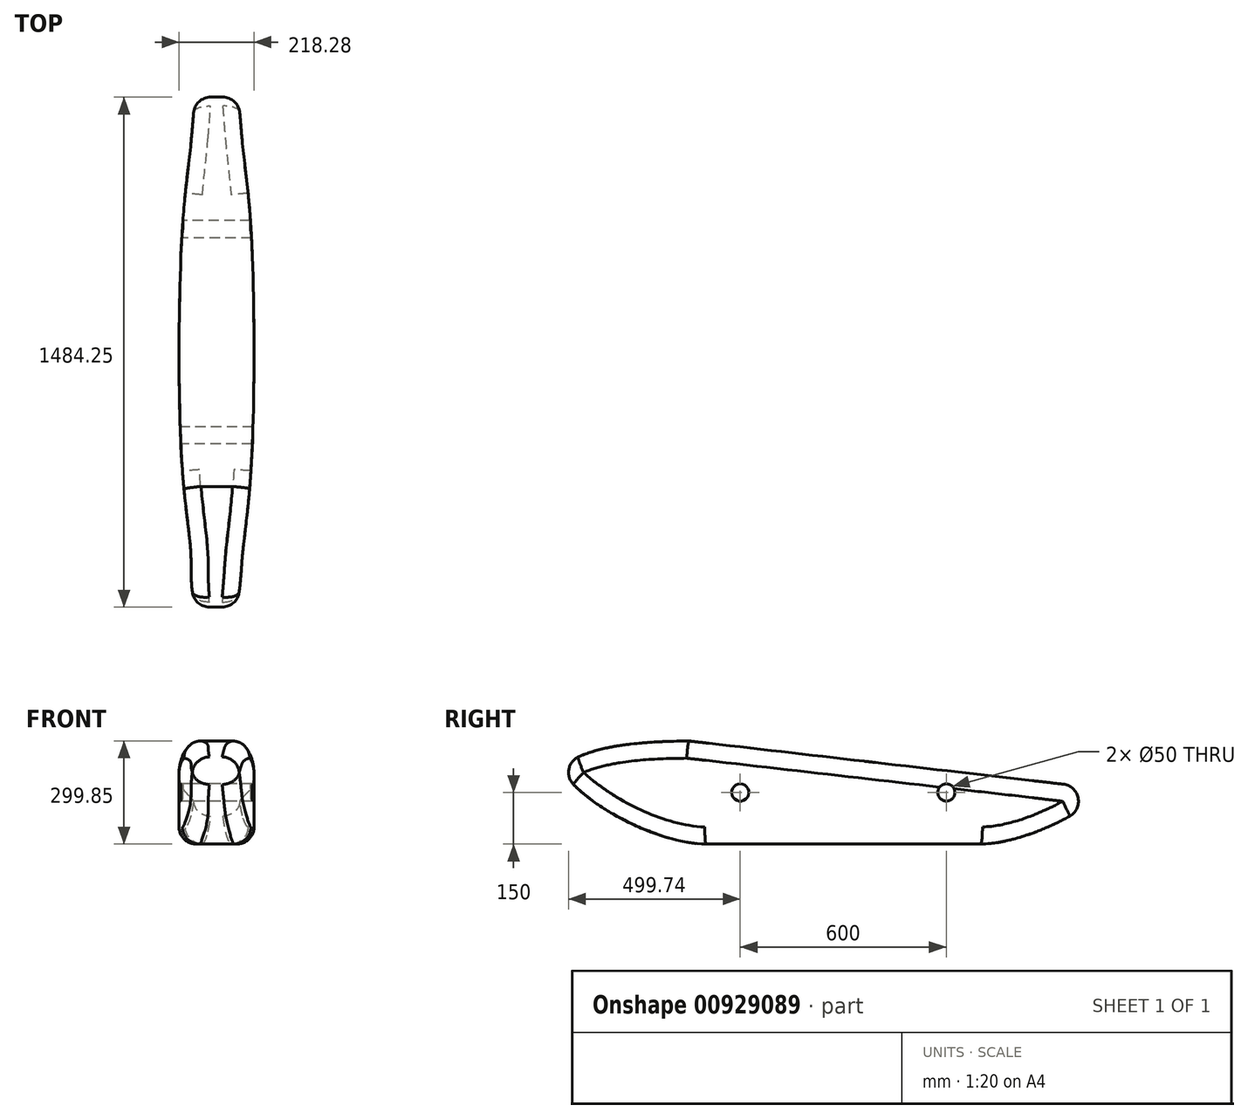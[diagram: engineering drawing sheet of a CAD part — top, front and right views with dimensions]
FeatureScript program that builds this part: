
annotation { "Feature Type Name" : "Feature", "Feature Type Description" : "" }
export const myFeature = defineFeature(function(context is Context, id is Id, definition is map)
    precondition{}
    {
        {
            var Q0;
            Q0=qCreatedBy(makeId("Top.planeOp"),FACE);
            var sketch = newSketch(context, id + "F0", { "sketchPlane" : qUnion([Q0])});
            skLineSegment(sketch, "E0", {"start": v(0, 0) * mm, "end": v(0, -1700) * mm});
            skLineSegment(sketch, "E1", {"start": v(-75, -300) * mm, "end": v(75, -300) * mm});
            skLineSegment(sketch, "E2", {"start": v(-75, -1500) * mm, "end": v(75, -1500) * mm});
            skLineSegment(sketch, "E3", {"start": v(-100, -550) * mm, "end": v(100, -550) * mm});
            skLineSegment(sketch, "E4", {"start": v(-100, -1250) * mm, "end": v(100, -1250) * mm});
            skLineSegment(sketch, "E5", {"start": v(-50, 0) * mm, "end": v(50, 0) * mm});
            skLineSegment(sketch, "E6", {"start": v(-50, -1700) * mm, "end": v(50, -1700) * mm});
            skFitSpline(sketch, "E7", {"points": [v(-50, -1700) * mm, v(-75, -1500) * mm, v(-100, -1250) * mm, v(-100, -550) * mm, v(-75, -300) * mm, v(-50, 0) * mm], "startDerivative": vector(-568.68, 1829.05) * mm, "endDerivative": vector(155.1, 1496.62) * mm});
            skFitSpline(sketch, "E8", {"points": [v(50, 0) * mm, v(75, -300) * mm, v(100, -550) * mm, v(100, -1250) * mm, v(75, -1500) * mm, v(50, -1700) * mm], "startDerivative": vector(155.1, -1496.62) * mm, "endDerivative": vector(-379.12, -1829.05) * mm});
            skSolve(sketch);
        }
        {
            var Q0;
            {var subQ0=sQuery(id+"F0.wireOp",EDGE,"E1");var subQ1=sQuery(id+"F0.wireOp",EDGE,"E0");var subQ2=makeQuery(id+"F0.imprint","INTERSECT",VERTEX,{"derivedFrom":[subQ1,subQ0]});Q0=makeQuery(id+"F0.imprint","IMPRINT",FACE,{"disambiguationData":[TD([[makeQuery(id+"F0.imprint","IMPRINT",EDGE,{"disambiguationData":[TD([[subQ2,1.0]])],"derivedFrom":subQ1}),1.0]])]});}
            var Q1;
            {var subQ0=sQuery(id+"F0.wireOp",EDGE,"E1");var subQ1=sQuery(id+"F0.wireOp",EDGE,"E0");var subQ2=makeQuery(id+"F0.imprint","INTERSECT",VERTEX,{"derivedFrom":[subQ1,subQ0]});Q1=makeQuery(id+"F0.imprint","IMPRINT",FACE,{"disambiguationData":[TD([[makeQuery(id+"F0.imprint","IMPRINT",EDGE,{"disambiguationData":[TD([[subQ2,1.0]])],"derivedFrom":subQ1}),-1.0]])]});}
            var Q2;
            {var subQ0=sQuery(id+"F0.wireOp",EDGE,"E1");var subQ1=sQuery(id+"F0.wireOp",EDGE,"E0");var subQ2=makeQuery(id+"F0.imprint","INTERSECT",VERTEX,{"derivedFrom":[subQ1,subQ0]});Q2=makeQuery(id+"F0.imprint","IMPRINT",FACE,{"disambiguationData":[TD([[makeQuery(id+"F0.imprint","IMPRINT",EDGE,{"disambiguationData":[TD([[subQ2,-1.0]])],"derivedFrom":subQ1}),-1.0]])]});}
            var Q3;
            {var subQ0=sQuery(id+"F0.wireOp",EDGE,"E1");var subQ1=sQuery(id+"F0.wireOp",EDGE,"E0");var subQ2=makeQuery(id+"F0.imprint","INTERSECT",VERTEX,{"derivedFrom":[subQ1,subQ0]});Q3=makeQuery(id+"F0.imprint","IMPRINT",FACE,{"disambiguationData":[TD([[makeQuery(id+"F0.imprint","IMPRINT",EDGE,{"disambiguationData":[TD([[subQ2,-1.0]])],"derivedFrom":subQ1}),1.0]])]});}
            var Q4;
            {var subQ0=sQuery(id+"F0.wireOp",EDGE,"E4");var subQ1=sQuery(id+"F0.wireOp",EDGE,"E0");var subQ2=makeQuery(id+"F0.imprint","INTERSECT",VERTEX,{"derivedFrom":[subQ1,subQ0]});Q4=makeQuery(id+"F0.imprint","IMPRINT",FACE,{"disambiguationData":[TD([[makeQuery(id+"F0.imprint","IMPRINT",EDGE,{"disambiguationData":[TD([[subQ2,1.0]])],"derivedFrom":subQ1}),-1.0]])]});}
            var Q5;
            {var subQ0=sQuery(id+"F0.wireOp",EDGE,"E4");var subQ1=sQuery(id+"F0.wireOp",EDGE,"E0");var subQ2=makeQuery(id+"F0.imprint","INTERSECT",VERTEX,{"derivedFrom":[subQ1,subQ0]});Q5=makeQuery(id+"F0.imprint","IMPRINT",FACE,{"disambiguationData":[TD([[makeQuery(id+"F0.imprint","IMPRINT",EDGE,{"disambiguationData":[TD([[subQ2,1.0]])],"derivedFrom":subQ1}),1.0]])]});}
            var Q6;
            {var subQ0=sQuery(id+"F0.wireOp",EDGE,"E4");var subQ1=sQuery(id+"F0.wireOp",EDGE,"E0");var subQ2=makeQuery(id+"F0.imprint","INTERSECT",VERTEX,{"derivedFrom":[subQ1,subQ0]});Q6=makeQuery(id+"F0.imprint","IMPRINT",FACE,{"disambiguationData":[TD([[makeQuery(id+"F0.imprint","IMPRINT",EDGE,{"disambiguationData":[TD([[subQ2,-1.0]])],"derivedFrom":subQ1}),-1.0]])]});}
            var Q7;
            {var subQ0=sQuery(id+"F0.wireOp",EDGE,"E4");var subQ1=sQuery(id+"F0.wireOp",EDGE,"E0");var subQ2=makeQuery(id+"F0.imprint","INTERSECT",VERTEX,{"derivedFrom":[subQ1,subQ0]});Q7=makeQuery(id+"F0.imprint","IMPRINT",FACE,{"disambiguationData":[TD([[makeQuery(id+"F0.imprint","IMPRINT",EDGE,{"disambiguationData":[TD([[subQ2,-1.0]])],"derivedFrom":subQ1}),1.0]])]});}
            var Q8;
            {var subQ0=sQuery(id+"F0.wireOp",EDGE,"E6");var subQ1=sQuery(id+"F0.wireOp",EDGE,"E0");var subQ2=makeQuery(id+"F0.imprint","INTERSECT",VERTEX,{"derivedFrom":[subQ1,subQ0]});Q8=makeQuery(id+"F0.imprint","IMPRINT",FACE,{"disambiguationData":[TD([[makeQuery(id+"F0.imprint","IMPRINT",EDGE,{"disambiguationData":[TD([[subQ2,1.0]])],"derivedFrom":subQ1}),-1.0]])]});}
            var Q9;
            {var subQ0=sQuery(id+"F0.wireOp",EDGE,"E6");var subQ1=sQuery(id+"F0.wireOp",EDGE,"E0");var subQ2=makeQuery(id+"F0.imprint","INTERSECT",VERTEX,{"derivedFrom":[subQ1,subQ0]});Q9=makeQuery(id+"F0.imprint","IMPRINT",FACE,{"disambiguationData":[TD([[makeQuery(id+"F0.imprint","IMPRINT",EDGE,{"disambiguationData":[TD([[subQ2,1.0]])],"derivedFrom":subQ1}),1.0]])]});}
            extrude(context, id + "F1", {"entities" : qUnion([Q0, Q1, Q2, Q3, Q4, Q5, Q6, Q7, Q8, Q9]), "depth" : 300 * mm, "offsetDistance" : 25 * mm});
        }
        {
            var Q0;
            Q0=qCreatedBy(makeId("Right.planeOp"),FACE);
            var sketch = newSketch(context, id + "F2", { "sketchPlane" : qUnion([Q0])});
            skLineSegment(sketch, "E9", {"start": v(0, 0) * mm, "end": v(-1700, 0) * mm});
            skLineSegment(sketch, "E10", {"start": v(-1700, 0) * mm, "end": v(-1700, 300) * mm});
            skLineSegment(sketch, "E11", {"start": v(-1700, 300) * mm, "end": v(0, 300) * mm});
            skLineSegment(sketch, "E12", {"start": v(0, 300) * mm, "end": v(0, 0) * mm});
            skFitSpline(sketch, "E13", {"points": [v(-450, 0) * mm, v(0, 300) * mm], "startDerivative": vector(450, 0) * mm, "endDerivative": vector(0, 450) * mm});
            skFitSpline(sketch, "E14", {"points": [v(-1250, 0) * mm, v(-1700, 300) * mm], "startDerivative": vector(-450, 0) * mm, "endDerivative": vector(0, 450) * mm});
            skFitSpline(sketch, "E15", {"points": [v(-1700, 150) * mm, v(-1250, 300) * mm], "startDerivative": vector(0, 450) * mm, "endDerivative": vector(450, 0) * mm});
            skFitSpline(sketch, "E16", {"points": [v(0, 0) * mm, v(-450, 300) * mm], "startDerivative": vector(0, 900) * mm, "endDerivative": vector(-450, 0) * mm});
            skSolve(sketch);
        }
        {
            var Q0;
            {var subQ0=sQuery(id+"F2.wireOp",EDGE,"E13");var subQ1=sQuery(id+"F2.wireOp",EDGE,"E9");var subQ2=makeQuery(id+"F2.imprint","INTERSECT",VERTEX,{"derivedFrom":[subQ1,subQ0]});Q0=makeQuery(id+"F2.imprint","IMPRINT",FACE,{"disambiguationData":[TD([[makeQuery(id+"F2.imprint","IMPRINT",EDGE,{"disambiguationData":[TD([[subQ2,-1.0]])],"derivedFrom":subQ0}),-1.0]])]});}
            var Q1;
            {var subQ0=sQuery(id+"F2.wireOp",EDGE,"E12");Q1=makeQuery(id+"F2.imprint","IMPRINT",FACE,{"disambiguationData":[TD([[makeQuery(id+"F2.imprint","IMPRINT",EDGE,{"derivedFrom":subQ0}),-1.0]])]});}
            var Q2;
            {var subQ1=sQuery(id+"F2.wireOp",EDGE,"E11");var subQ3=sQuery(id+"F2.wireOp",EDGE,"E16");var subQ4=makeQuery(id+"F2.imprint","INTERSECT",VERTEX,{"derivedFrom":[subQ1,subQ3]});Q2=makeQuery(id+"F2.imprint","IMPRINT",FACE,{"disambiguationData":[TD([[makeQuery(id+"F2.imprint","IMPRINT",EDGE,{"disambiguationData":[TD([[subQ4,1.0]])],"derivedFrom":subQ3}),-1.0]])]});}
            var Q3;
            {var subQ0=sQuery(id+"F2.wireOp",EDGE,"E14");var subQ1=sQuery(id+"F2.wireOp",EDGE,"E9");var subQ2=makeQuery(id+"F2.imprint","INTERSECT",VERTEX,{"derivedFrom":[subQ1,subQ0]});Q3=makeQuery(id+"F2.imprint","IMPRINT",FACE,{"disambiguationData":[TD([[makeQuery(id+"F2.imprint","IMPRINT",EDGE,{"disambiguationData":[TD([[subQ2,-1.0]])],"derivedFrom":subQ1}),-1.0]])]});}
            var Q4;
            {var subQ0=sQuery(id+"F2.wireOp",EDGE,"E15");var subQ1=sQuery(id+"F2.wireOp",EDGE,"E10");var subQ2=makeQuery(id+"F2.imprint","INTERSECT",VERTEX,{"derivedFrom":[subQ1,subQ0]});Q4=makeQuery(id+"F2.imprint","IMPRINT",FACE,{"disambiguationData":[TD([[makeQuery(id+"F2.imprint","IMPRINT",EDGE,{"disambiguationData":[TD([[subQ2,-1.0]])],"derivedFrom":subQ0}),1.0]])]});}
            var Q5;
            {var subQ0=sQuery(id+"F2.wireOp",EDGE,"E15");var subQ1=sQuery(id+"F2.wireOp",EDGE,"E11");var subQ2=makeQuery(id+"F2.imprint","INTERSECT",VERTEX,{"derivedFrom":[subQ1,subQ0]});Q5=makeQuery(id+"F2.imprint","IMPRINT",FACE,{"disambiguationData":[TD([[makeQuery(id+"F2.imprint","IMPRINT",EDGE,{"disambiguationData":[TD([[subQ2,1.0]])],"derivedFrom":subQ0}),1.0]])]});}
            extrude(context, id + "F3", {"entities" : qUnion([Q0, Q1, Q2, Q3, Q4, Q5]), "operationType" : NewBodyOperationType.REMOVE, "endBound" : BoundingType.SYMMETRIC, "oppositeDirection" : true, "depth" : 350 * mm, "offsetDistance" : 25 * mm});
        }
        {
            var Q0;
            {var subQ0=sQuery(id+"F0.wireOp",EDGE,"E8");Q0=makeQuery(id+"F3.boolean.opBoolean","INTERSECT",EDGE,{"derivedFrom":[makeQuery(id+"F1.opExtrude","SWEPT_FACE",FACE,{"disambiguationData":[OSD([subQ0]),TDD([makeQuery(id+"F0.imprint","IMPRINT",EDGE,{"disambiguationData":[TD([[makeQuery(id+"F0.imprint","INTERSECT",VERTEX,{"derivedFrom":[sQuery(id+"F0.wireOp",EDGE,"E2"),subQ0]}),-1.0]])],"derivedFrom":subQ0})])]}),makeQuery(id+"F3.opExtrude","SWEPT_FACE",FACE,{"disambiguationData":[OSD([sQuery(id+"F2.wireOp",EDGE,"E14")])]})]});}
            var Q1;
            {var subQ0=sQuery(id+"F0.wireOp",EDGE,"E8");Q1=makeQuery(id+"F1.opExtrude","CAP_EDGE",EDGE,{"disambiguationData":[OSD([subQ0]),TDD([makeQuery(id+"F0.imprint","IMPRINT",EDGE,{"disambiguationData":[TD([[makeQuery(id+"F0.imprint","INTERSECT",VERTEX,{"derivedFrom":[sQuery(id+"F0.wireOp",EDGE,"E2"),subQ0]}),1.0]])],"derivedFrom":subQ0})])],"isStart":true});}
            var Q2;
            {var subQ0=sQuery(id+"F0.wireOp",EDGE,"E8");Q2=makeQuery(id+"F1.opExtrude","CAP_EDGE",EDGE,{"disambiguationData":[OSD([subQ0]),TDD([makeQuery(id+"F0.imprint","IMPRINT",EDGE,{"disambiguationData":[TD([[makeQuery(id+"F0.imprint","INTERSECT",VERTEX,{"derivedFrom":[sQuery(id+"F0.wireOp",EDGE,"E2"),subQ0]}),-1.0]])],"derivedFrom":subQ0})])],"isStart":true});}
            var Q3;
            {var subQ0=sQuery(id+"F0.wireOp",EDGE,"E8");Q3=makeQuery(id+"F1.opExtrude","CAP_EDGE",EDGE,{"disambiguationData":[OSD([subQ0]),TDD([makeQuery(id+"F0.imprint","IMPRINT",EDGE,{"disambiguationData":[TD([[makeQuery(id+"F0.imprint","INTERSECT",VERTEX,{"derivedFrom":[sQuery(id+"F0.wireOp",EDGE,"E4"),subQ0]}),1.0]])],"derivedFrom":subQ0})])],"isStart":true});}
            var Q4;
            {var subQ0=sQuery(id+"F0.wireOp",EDGE,"E8");Q4=makeQuery(id+"F1.opExtrude","CAP_EDGE",EDGE,{"disambiguationData":[OSD([subQ0]),TDD([makeQuery(id+"F0.imprint","IMPRINT",EDGE,{"disambiguationData":[TD([[makeQuery(id+"F0.imprint","INTERSECT",VERTEX,{"derivedFrom":[sQuery(id+"F0.wireOp",EDGE,"E1"),subQ0]}),-1.0]])],"derivedFrom":subQ0})])],"isStart":true});}
            var Q5;
            {var subQ0=sQuery(id+"F0.wireOp",EDGE,"E8");Q5=makeQuery(id+"F1.opExtrude","CAP_EDGE",EDGE,{"disambiguationData":[OSD([subQ0]),TDD([makeQuery(id+"F0.imprint","IMPRINT",EDGE,{"disambiguationData":[TD([[makeQuery(id+"F0.imprint","INTERSECT",VERTEX,{"derivedFrom":[sQuery(id+"F0.wireOp",EDGE,"E1"),subQ0]}),1.0]])],"derivedFrom":subQ0})])],"isStart":true});}
            var Q6;
            {var subQ0=sQuery(id+"F0.wireOp",EDGE,"E8");Q6=makeQuery(id+"F3.boolean.opBoolean","INTERSECT",EDGE,{"derivedFrom":[makeQuery(id+"F1.opExtrude","SWEPT_FACE",FACE,{"disambiguationData":[OSD([subQ0]),TDD([makeQuery(id+"F0.imprint","IMPRINT",EDGE,{"disambiguationData":[TD([[makeQuery(id+"F0.imprint","INTERSECT",VERTEX,{"derivedFrom":[sQuery(id+"F0.wireOp",EDGE,"E1"),subQ0]}),1.0]])],"derivedFrom":subQ0})])]}),makeQuery(id+"F3.opExtrude","SWEPT_FACE",FACE,{"disambiguationData":[OSD([sQuery(id+"F2.wireOp",EDGE,"E13")])]})]});}
            var Q7;
            {var subQ0=sQuery(id+"F0.wireOp",EDGE,"E7");Q7=makeQuery(id+"F3.boolean.opBoolean","INTERSECT",EDGE,{"derivedFrom":[makeQuery(id+"F1.opExtrude","SWEPT_FACE",FACE,{"disambiguationData":[OSD([subQ0]),TDD([makeQuery(id+"F0.imprint","IMPRINT",EDGE,{"disambiguationData":[TD([[makeQuery(id+"F0.imprint","INTERSECT",VERTEX,{"derivedFrom":[sQuery(id+"F0.wireOp",EDGE,"E2"),subQ0]}),1.0]])],"derivedFrom":subQ0})])]}),makeQuery(id+"F3.opExtrude","SWEPT_FACE",FACE,{"disambiguationData":[OSD([sQuery(id+"F2.wireOp",EDGE,"E14")])]})]});}
            var Q8;
            {var subQ0=sQuery(id+"F0.wireOp",EDGE,"E7");Q8=makeQuery(id+"F1.opExtrude","CAP_EDGE",EDGE,{"disambiguationData":[OSD([subQ0]),TDD([makeQuery(id+"F0.imprint","IMPRINT",EDGE,{"disambiguationData":[TD([[makeQuery(id+"F0.imprint","INTERSECT",VERTEX,{"derivedFrom":[sQuery(id+"F0.wireOp",EDGE,"E2"),subQ0]}),1.0]])],"derivedFrom":subQ0})])],"isStart":true});}
            var Q9;
            {var subQ0=sQuery(id+"F0.wireOp",EDGE,"E7");Q9=makeQuery(id+"F1.opExtrude","CAP_EDGE",EDGE,{"disambiguationData":[OSD([subQ0]),TDD([makeQuery(id+"F0.imprint","IMPRINT",EDGE,{"disambiguationData":[TD([[makeQuery(id+"F0.imprint","INTERSECT",VERTEX,{"derivedFrom":[sQuery(id+"F0.wireOp",EDGE,"E2"),subQ0]}),-1.0]])],"derivedFrom":subQ0})])],"isStart":true});}
            var Q10;
            {var subQ0=sQuery(id+"F0.wireOp",EDGE,"E7");Q10=makeQuery(id+"F1.opExtrude","CAP_EDGE",EDGE,{"disambiguationData":[OSD([subQ0]),TDD([makeQuery(id+"F0.imprint","IMPRINT",EDGE,{"disambiguationData":[TD([[makeQuery(id+"F0.imprint","INTERSECT",VERTEX,{"derivedFrom":[sQuery(id+"F0.wireOp",EDGE,"E4"),subQ0]}),-1.0]])],"derivedFrom":subQ0})])],"isStart":true});}
            var Q11;
            {var subQ0=sQuery(id+"F0.wireOp",EDGE,"E7");Q11=makeQuery(id+"F1.opExtrude","CAP_EDGE",EDGE,{"disambiguationData":[OSD([subQ0]),TDD([makeQuery(id+"F0.imprint","IMPRINT",EDGE,{"disambiguationData":[TD([[makeQuery(id+"F0.imprint","INTERSECT",VERTEX,{"derivedFrom":[sQuery(id+"F0.wireOp",EDGE,"E1"),subQ0]}),1.0]])],"derivedFrom":subQ0})])],"isStart":true});}
            var Q12;
            {var subQ0=sQuery(id+"F0.wireOp",EDGE,"E7");Q12=makeQuery(id+"F1.opExtrude","CAP_EDGE",EDGE,{"disambiguationData":[OSD([subQ0]),TDD([makeQuery(id+"F0.imprint","IMPRINT",EDGE,{"disambiguationData":[TD([[makeQuery(id+"F0.imprint","INTERSECT",VERTEX,{"derivedFrom":[sQuery(id+"F0.wireOp",EDGE,"E1"),subQ0]}),-1.0]])],"derivedFrom":subQ0})])],"isStart":true});}
            var Q13;
            {var subQ0=sQuery(id+"F0.wireOp",EDGE,"E7");Q13=makeQuery(id+"F3.boolean.opBoolean","INTERSECT",EDGE,{"derivedFrom":[makeQuery(id+"F1.opExtrude","SWEPT_FACE",FACE,{"disambiguationData":[OSD([subQ0]),TDD([makeQuery(id+"F0.imprint","IMPRINT",EDGE,{"disambiguationData":[TD([[makeQuery(id+"F0.imprint","INTERSECT",VERTEX,{"derivedFrom":[sQuery(id+"F0.wireOp",EDGE,"E1"),subQ0]}),-1.0]])],"derivedFrom":subQ0})])]}),makeQuery(id+"F3.opExtrude","SWEPT_FACE",FACE,{"disambiguationData":[OSD([sQuery(id+"F2.wireOp",EDGE,"E13")])]})]});}
            fillet(context, id + "F4", {"entities" : qUnion([Q0, Q1, Q2, Q3, Q4, Q5, Q6, Q7, Q8, Q9, Q10, Q11, Q12, Q13]), "tangentPropagation" : true, "radius" : 50 * mm, "defaultsChanged" : true, "vertexSettings" : [], "allowEdgeOverflow" : false});
        }
        {
            var Q0;
            Q0=qCreatedBy(makeId("Right.planeOp"),FACE);
            var sketch = newSketch(context, id + "F5", { "sketchPlane" : qUnion([Q0])});
            skCircle(sketch, "E17", {"center": v(-550, 150) * mm, "radius": 25 * mm});
            skCircle(sketch, "E18", {"center": v(-1150, 150) * mm, "radius": 25 * mm});
            skSolve(sketch);
        }
        {
            var Q0;
            Q0 = qSketchRegion(id + "F5", true);
            extrude(context, id + "F6", {"entities" : qUnion([Q0]), "operationType" : NewBodyOperationType.REMOVE, "endBound" : BoundingType.SYMMETRIC, "depth" : 350 * mm, "offsetDistance" : 25 * mm});
        }
        {
            var Q0;
            Q0=qCreatedBy(makeId("Right.planeOp"),FACE);
            var sketch = newSketch(context, id + "F7", { "sketchPlane" : qUnion([Q0])});
            skLineSegment(sketch, "E19", {"start": v(0, 0) * mm, "end": v(-1700, 0) * mm});
            skLineSegment(sketch, "E20", {"start": v(-1700, 0) * mm, "end": v(-1700, 300) * mm});
            skLineSegment(sketch, "E21", {"start": v(-1700, 300) * mm, "end": v(0, 300) * mm});
            skLineSegment(sketch, "E22", {"start": v(0, 300) * mm, "end": v(0, 0) * mm});
            skLineSegment(sketch, "E23", {"start": v(-1300, 300) * mm, "end": v(0, 150) * mm});
            skSolve(sketch);
        }
        {
            var Q0;
            {var subQ0=sQuery(id+"F7.wireOp",EDGE,"NQDjfycC-HldQ-nqyw-sXny-62I867NfjnbV");Q0=makeQuery(id+"F7.imprint","IMPRINT",FACE,{"disambiguationData":[TD([[makeQuery(id+"F7.imprint","IMPRINT",EDGE,{"derivedFrom":subQ0}),-1.0]])]});}
            var Q1;
            {var subQ0=sQuery(id+"F7.wireOp",EDGE,"E23");Q1=makeQuery(id+"F7.imprint","IMPRINT",FACE,{"disambiguationData":[TD([[makeQuery(id+"F7.imprint","IMPRINT",EDGE,{"derivedFrom":subQ0}),1.0]])]});}
            extrude(context, id + "F8", {"entities" : qUnion([Q0, Q1]), "operationType" : NewBodyOperationType.REMOVE, "endBound" : BoundingType.SYMMETRIC, "oppositeDirection" : true, "depth" : 350 * mm, "offsetDistance" : 25 * mm});
        }
        {
            var Q0;
            {var subQ0=sQuery(id+"F0.wireOp",EDGE,"E8");Q0=makeQuery(id+"F3.boolean.opBoolean","INTERSECT",EDGE,{"derivedFrom":[makeQuery(id+"F1.opExtrude","SWEPT_FACE",FACE,{"disambiguationData":[OSD([subQ0]),TDD([makeQuery(id+"F0.imprint","IMPRINT",EDGE,{"disambiguationData":[TD([[makeQuery(id+"F0.imprint","INTERSECT",VERTEX,{"derivedFrom":[sQuery(id+"F0.wireOp",EDGE,"E2"),subQ0]}),-1.0]])],"derivedFrom":subQ0})])]}),makeQuery(id+"F3.opExtrude","SWEPT_FACE",FACE,{"disambiguationData":[OSD([sQuery(id+"F2.wireOp",EDGE,"E15")])]})]});}
            var Q1;
            {var subQ0=sQuery(id+"F0.wireOp",EDGE,"E8");Q1=makeQuery(id+"F4.opFillet","BLEND_EDGE",EDGE,{"blendedFrom":[makeQuery(id+"F3.boolean.opBoolean","INTERSECT",EDGE,{"derivedFrom":[makeQuery(id+"F1.opExtrude","SWEPT_FACE",FACE,{"disambiguationData":[OSD([subQ0]),TDD([makeQuery(id+"F0.imprint","IMPRINT",EDGE,{"disambiguationData":[TD([[makeQuery(id+"F0.imprint","INTERSECT",VERTEX,{"derivedFrom":[sQuery(id+"F0.wireOp",EDGE,"E2"),subQ0]}),-1.0]])],"derivedFrom":subQ0})])]}),makeQuery(id+"F3.opExtrude","SWEPT_FACE",FACE,{"disambiguationData":[OSD([sQuery(id+"F2.wireOp",EDGE,"E14")])]})]}),makeQuery(id+"F3.boolean.opBoolean","COPY",FACE,{"derivedFrom":makeQuery(id+"F3.opExtrude","SWEPT_FACE",FACE,{"disambiguationData":[OSD([sQuery(id+"F2.wireOp",EDGE,"E15")])]})})],"blendedInto":[makeQuery(id+"F3.boolean.opBoolean","COPY",FACE,{"derivedFrom":makeQuery(id+"F3.opExtrude","SWEPT_FACE",FACE,{"disambiguationData":[OSD([sQuery(id+"F2.wireOp",EDGE,"E15")])]})})]});}
            var Q2;
            {var subQ0=sQuery(id+"F0.wireOp",EDGE,"E7");Q2=makeQuery(id+"F4.opFillet","BLEND_EDGE",EDGE,{"blendedFrom":[makeQuery(id+"F3.boolean.opBoolean","INTERSECT",EDGE,{"derivedFrom":[makeQuery(id+"F1.opExtrude","SWEPT_FACE",FACE,{"disambiguationData":[OSD([subQ0]),TDD([makeQuery(id+"F0.imprint","IMPRINT",EDGE,{"disambiguationData":[TD([[makeQuery(id+"F0.imprint","INTERSECT",VERTEX,{"derivedFrom":[sQuery(id+"F0.wireOp",EDGE,"E2"),subQ0]}),1.0]])],"derivedFrom":subQ0})])]}),makeQuery(id+"F3.opExtrude","SWEPT_FACE",FACE,{"disambiguationData":[OSD([sQuery(id+"F2.wireOp",EDGE,"E14")])]})]}),makeQuery(id+"F3.boolean.opBoolean","COPY",FACE,{"derivedFrom":makeQuery(id+"F3.opExtrude","SWEPT_FACE",FACE,{"disambiguationData":[OSD([sQuery(id+"F2.wireOp",EDGE,"E15")])]})})],"blendedInto":[makeQuery(id+"F3.boolean.opBoolean","COPY",FACE,{"derivedFrom":makeQuery(id+"F3.opExtrude","SWEPT_FACE",FACE,{"disambiguationData":[OSD([sQuery(id+"F2.wireOp",EDGE,"E15")])]})})]});}
            var Q3;
            {var subQ0=sQuery(id+"F0.wireOp",EDGE,"E7");Q3=makeQuery(id+"F3.boolean.opBoolean","INTERSECT",EDGE,{"derivedFrom":[makeQuery(id+"F1.opExtrude","SWEPT_FACE",FACE,{"disambiguationData":[OSD([subQ0]),TDD([makeQuery(id+"F0.imprint","IMPRINT",EDGE,{"disambiguationData":[TD([[makeQuery(id+"F0.imprint","INTERSECT",VERTEX,{"derivedFrom":[sQuery(id+"F0.wireOp",EDGE,"E2"),subQ0]}),1.0]])],"derivedFrom":subQ0})])]}),makeQuery(id+"F3.opExtrude","SWEPT_FACE",FACE,{"disambiguationData":[OSD([sQuery(id+"F2.wireOp",EDGE,"E15")])]})]});}
            var Q4;
            {var subQ0=sQuery(id+"F0.wireOp",EDGE,"E7");Q4=makeQuery(id+"F8.boolean.opBoolean","INTERSECT",EDGE,{"derivedFrom":[makeQuery(id+"F1.opExtrude","SWEPT_FACE",FACE,{"disambiguationData":[OSD([subQ0]),TDD([makeQuery(id+"F0.imprint","IMPRINT",EDGE,{"disambiguationData":[TD([[makeQuery(id+"F0.imprint","INTERSECT",VERTEX,{"derivedFrom":[sQuery(id+"F0.wireOp",EDGE,"E2"),subQ0]}),-1.0]])],"derivedFrom":subQ0})])]}),makeQuery(id+"F8.opExtrude","SWEPT_FACE",FACE,{"disambiguationData":[OSD([sQuery(id+"F7.wireOp",EDGE,"E23")])]})]});}
            var Q5;
            {var subQ0=sQuery(id+"F0.wireOp",EDGE,"E8");Q5=makeQuery(id+"F8.boolean.opBoolean","INTERSECT",EDGE,{"derivedFrom":[makeQuery(id+"F1.opExtrude","SWEPT_FACE",FACE,{"disambiguationData":[OSD([subQ0]),TDD([makeQuery(id+"F0.imprint","IMPRINT",EDGE,{"disambiguationData":[TD([[makeQuery(id+"F0.imprint","INTERSECT",VERTEX,{"derivedFrom":[sQuery(id+"F0.wireOp",EDGE,"E2"),subQ0]}),1.0]])],"derivedFrom":subQ0})])]}),makeQuery(id+"F8.opExtrude","SWEPT_FACE",FACE,{"disambiguationData":[OSD([sQuery(id+"F7.wireOp",EDGE,"E23")])]})]});}
            var Q6;
            {var subQ0=sQuery(id+"F0.wireOp",EDGE,"E8");Q6=makeQuery(id+"F8.boolean.opBoolean","INTERSECT",EDGE,{"derivedFrom":[makeQuery(id+"F1.opExtrude","SWEPT_FACE",FACE,{"disambiguationData":[OSD([subQ0]),TDD([makeQuery(id+"F0.imprint","IMPRINT",EDGE,{"disambiguationData":[TD([[makeQuery(id+"F0.imprint","INTERSECT",VERTEX,{"derivedFrom":[sQuery(id+"F0.wireOp",EDGE,"E3"),subQ0]}),-1.0]])],"derivedFrom":subQ0})])]}),makeQuery(id+"F8.opExtrude","SWEPT_FACE",FACE,{"disambiguationData":[OSD([sQuery(id+"F7.wireOp",EDGE,"E23")])]})]});}
            var Q7;
            {var subQ0=sQuery(id+"F0.wireOp",EDGE,"E8");Q7=makeQuery(id+"F8.boolean.opBoolean","INTERSECT",EDGE,{"derivedFrom":[makeQuery(id+"F1.opExtrude","SWEPT_FACE",FACE,{"disambiguationData":[OSD([subQ0]),TDD([makeQuery(id+"F0.imprint","IMPRINT",EDGE,{"disambiguationData":[TD([[makeQuery(id+"F0.imprint","INTERSECT",VERTEX,{"derivedFrom":[sQuery(id+"F0.wireOp",EDGE,"E1"),subQ0]}),-1.0]])],"derivedFrom":subQ0})])]}),makeQuery(id+"F8.opExtrude","SWEPT_FACE",FACE,{"disambiguationData":[OSD([sQuery(id+"F7.wireOp",EDGE,"E23")])]})]});}
            var Q8;
            {var subQ0=sQuery(id+"F0.wireOp",EDGE,"E8");Q8=makeQuery(id+"F8.boolean.opBoolean","INTERSECT",EDGE,{"derivedFrom":[makeQuery(id+"F1.opExtrude","SWEPT_FACE",FACE,{"disambiguationData":[OSD([subQ0]),TDD([makeQuery(id+"F0.imprint","IMPRINT",EDGE,{"disambiguationData":[TD([[makeQuery(id+"F0.imprint","INTERSECT",VERTEX,{"derivedFrom":[sQuery(id+"F0.wireOp",EDGE,"E1"),subQ0]}),1.0]])],"derivedFrom":subQ0})])]}),makeQuery(id+"F8.opExtrude","SWEPT_FACE",FACE,{"disambiguationData":[OSD([sQuery(id+"F7.wireOp",EDGE,"E23")])]})]});}
            var Q9;
            {var subQ0=sQuery(id+"F2.wireOp",EDGE,"E13");var subQ1=sQuery(id+"F0.wireOp",EDGE,"E8");Q9=makeQuery(id+"F8.boolean.opBoolean","INTERSECT",EDGE,{"derivedFrom":[makeQuery(id+"F4.opFillet","BLEND_FACE",FACE,{"disambiguationData":[OSD([subQ1,subQ0]),TDD([makeQuery(id+"F3.boolean.opBoolean","INTERSECT",EDGE,{"derivedFrom":[makeQuery(id+"F1.opExtrude","SWEPT_FACE",FACE,{"disambiguationData":[OSD([subQ1]),TDD([makeQuery(id+"F0.imprint","IMPRINT",EDGE,{"disambiguationData":[TD([[makeQuery(id+"F0.imprint","INTERSECT",VERTEX,{"derivedFrom":[sQuery(id+"F0.wireOp",EDGE,"E1"),subQ1]}),1.0]])],"derivedFrom":subQ1})])]}),makeQuery(id+"F3.opExtrude","SWEPT_FACE",FACE,{"disambiguationData":[OSD([subQ0])]})]})])]}),makeQuery(id+"F8.opExtrude","SWEPT_FACE",FACE,{"disambiguationData":[OSD([sQuery(id+"F7.wireOp",EDGE,"E23")])]})]});}
            var Q10;
            {var subQ0=sQuery(id+"F0.wireOp",EDGE,"E7");Q10=makeQuery(id+"F8.boolean.opBoolean","INTERSECT",EDGE,{"derivedFrom":[makeQuery(id+"F1.opExtrude","SWEPT_FACE",FACE,{"disambiguationData":[OSD([subQ0]),TDD([makeQuery(id+"F0.imprint","IMPRINT",EDGE,{"disambiguationData":[TD([[makeQuery(id+"F0.imprint","INTERSECT",VERTEX,{"derivedFrom":[sQuery(id+"F0.wireOp",EDGE,"E1"),subQ0]}),-1.0]])],"derivedFrom":subQ0})])]}),makeQuery(id+"F8.opExtrude","SWEPT_FACE",FACE,{"disambiguationData":[OSD([sQuery(id+"F7.wireOp",EDGE,"E23")])]})]});}
            var Q11;
            {var subQ0=sQuery(id+"F0.wireOp",EDGE,"E7");Q11=makeQuery(id+"F8.boolean.opBoolean","INTERSECT",EDGE,{"derivedFrom":[makeQuery(id+"F1.opExtrude","SWEPT_FACE",FACE,{"disambiguationData":[OSD([subQ0]),TDD([makeQuery(id+"F0.imprint","IMPRINT",EDGE,{"disambiguationData":[TD([[makeQuery(id+"F0.imprint","INTERSECT",VERTEX,{"derivedFrom":[sQuery(id+"F0.wireOp",EDGE,"E3"),subQ0]}),1.0]])],"derivedFrom":subQ0})])]}),makeQuery(id+"F8.opExtrude","SWEPT_FACE",FACE,{"disambiguationData":[OSD([sQuery(id+"F7.wireOp",EDGE,"E23")])]})]});}
            var Q12;
            {var subQ0=sQuery(id+"F0.wireOp",EDGE,"E7");Q12=makeQuery(id+"F8.boolean.opBoolean","INTERSECT",EDGE,{"derivedFrom":[makeQuery(id+"F1.opExtrude","SWEPT_FACE",FACE,{"disambiguationData":[OSD([subQ0]),TDD([makeQuery(id+"F0.imprint","IMPRINT",EDGE,{"disambiguationData":[TD([[makeQuery(id+"F0.imprint","INTERSECT",VERTEX,{"derivedFrom":[sQuery(id+"F0.wireOp",EDGE,"E1"),subQ0]}),1.0]])],"derivedFrom":subQ0})])]}),makeQuery(id+"F8.opExtrude","SWEPT_FACE",FACE,{"disambiguationData":[OSD([sQuery(id+"F7.wireOp",EDGE,"E23")])]})]});}
            var Q13;
            {var subQ0=sQuery(id+"F2.wireOp",EDGE,"E13");var subQ1=sQuery(id+"F0.wireOp",EDGE,"E8");Q13=makeQuery(id+"F15f9usm6Ppsztq_1.boolean.opBoolean","INTERSECT",EDGE,{"derivedFrom":[makeQuery(id+"F4.opFillet","BLEND_FACE",FACE,{"disambiguationData":[OSD([subQ1,subQ0]),TDD([makeQuery(id+"F3.boolean.opBoolean","INTERSECT",EDGE,{"derivedFrom":[makeQuery(id+"F1.opExtrude","SWEPT_FACE",FACE,{"disambiguationData":[OSD([subQ1]),TDD([makeQuery(id+"F0.imprint","IMPRINT",EDGE,{"disambiguationData":[TD([[makeQuery(id+"F0.imprint","INTERSECT",VERTEX,{"derivedFrom":[sQuery(id+"F0.wireOp",EDGE,"E1"),subQ1]}),1.0]])],"derivedFrom":subQ1})])]}),makeQuery(id+"F3.opExtrude","SWEPT_FACE",FACE,{"disambiguationData":[OSD([subQ0])]})]})])]}),makeQuery(id+"F15f9usm6Ppsztq_1.opExtrude","SWEPT_FACE",FACE,{"disambiguationData":[OSD([sQuery(id+"F4Mq11ggPU0jxlY_1.wireOp",EDGE,"IhQiX8d1-Yl78-15A5-HocH-n7skXIkgdIrg")])]})]});}
            var Q14;
            {var subQ0=sQuery(id+"F2.wireOp",EDGE,"E13");var subQ1=sQuery(id+"F0.wireOp",EDGE,"E7");Q14=makeQuery(id+"F15f9usm6Ppsztq_1.boolean.opBoolean","INTERSECT",EDGE,{"derivedFrom":[makeQuery(id+"F4.opFillet","BLEND_FACE",FACE,{"disambiguationData":[OSD([subQ1,subQ0]),TDD([makeQuery(id+"F3.boolean.opBoolean","INTERSECT",EDGE,{"derivedFrom":[makeQuery(id+"F1.opExtrude","SWEPT_FACE",FACE,{"disambiguationData":[OSD([subQ1]),TDD([makeQuery(id+"F0.imprint","IMPRINT",EDGE,{"disambiguationData":[TD([[makeQuery(id+"F0.imprint","INTERSECT",VERTEX,{"derivedFrom":[sQuery(id+"F0.wireOp",EDGE,"E1"),subQ1]}),-1.0]])],"derivedFrom":subQ1})])]}),makeQuery(id+"F3.opExtrude","SWEPT_FACE",FACE,{"disambiguationData":[OSD([subQ0])]})]})])]}),makeQuery(id+"F15f9usm6Ppsztq_1.opExtrude","SWEPT_FACE",FACE,{"disambiguationData":[OSD([sQuery(id+"F4Mq11ggPU0jxlY_1.wireOp",EDGE,"IhQiX8d1-Yl78-15A5-HocH-n7skXIkgdIrg")])]})]});}
            var Q15;
            {var subQ0=sQuery(id+"F0.wireOp",EDGE,"E8");Q15=makeQuery(id+"F3.boolean.opBoolean","INTERSECT",EDGE,{"derivedFrom":[makeQuery(id+"F1.opExtrude","SWEPT_FACE",FACE,{"disambiguationData":[OSD([subQ0]),TDD([makeQuery(id+"F0.imprint","IMPRINT",EDGE,{"disambiguationData":[TD([[makeQuery(id+"F0.imprint","INTERSECT",VERTEX,{"derivedFrom":[sQuery(id+"F0.wireOp",EDGE,"E2"),subQ0]}),1.0]])],"derivedFrom":subQ0})])]}),makeQuery(id+"F3.opExtrude","SWEPT_FACE",FACE,{"disambiguationData":[OSD([sQuery(id+"F2.wireOp",EDGE,"E15")])]})]});}
            var Q16;
            {var subQ0=sQuery(id+"F0.wireOp",EDGE,"E7");Q16=makeQuery(id+"F3.boolean.opBoolean","INTERSECT",EDGE,{"derivedFrom":[makeQuery(id+"F1.opExtrude","SWEPT_FACE",FACE,{"disambiguationData":[OSD([subQ0]),TDD([makeQuery(id+"F0.imprint","IMPRINT",EDGE,{"disambiguationData":[TD([[makeQuery(id+"F0.imprint","INTERSECT",VERTEX,{"derivedFrom":[sQuery(id+"F0.wireOp",EDGE,"E2"),subQ0]}),-1.0]])],"derivedFrom":subQ0})])]}),makeQuery(id+"F3.opExtrude","SWEPT_FACE",FACE,{"disambiguationData":[OSD([sQuery(id+"F2.wireOp",EDGE,"E15")])]})]});}
            var Q17;
            Q17=makeQuery(id+"F15f9usm6Ppsztq_1.boolean.opBoolean","INTERSECT",EDGE,{"derivedFrom":[makeQuery(id+"F3.boolean.opBoolean","COPY",FACE,{"derivedFrom":makeQuery(id+"F3.opExtrude","SWEPT_FACE",FACE,{"disambiguationData":[OSD([sQuery(id+"F2.wireOp",EDGE,"E13")])]})}),makeQuery(id+"F15f9usm6Ppsztq_1.opExtrude","SWEPT_FACE",FACE,{"disambiguationData":[OSD([sQuery(id+"F4Mq11ggPU0jxlY_1.wireOp",EDGE,"IhQiX8d1-Yl78-15A5-HocH-n7skXIkgdIrg")])]})]});
            var Q18;
            Q18=makeQuery(id+"F3.boolean.opBoolean","COPY",EDGE,{"derivedFrom":makeQuery(id+"F3.opExtrude","SWEPT_EDGE",EDGE,{"disambiguationData":[OSD([sQuery(id+"F2.wireOp",EDGE,"E14"),sQuery(id+"F2.wireOp",EDGE,"E15")])]})});
            var Q19;
            {var subQ0=sQuery(id+"F2.wireOp",EDGE,"E13");var subQ1=sQuery(id+"F0.wireOp",EDGE,"E7");Q19=makeQuery(id+"F8.boolean.opBoolean","INTERSECT",EDGE,{"derivedFrom":[makeQuery(id+"F4.opFillet","BLEND_FACE",FACE,{"disambiguationData":[OSD([subQ1,subQ0]),TDD([makeQuery(id+"F3.boolean.opBoolean","INTERSECT",EDGE,{"derivedFrom":[makeQuery(id+"F1.opExtrude","SWEPT_FACE",FACE,{"disambiguationData":[OSD([subQ1]),TDD([makeQuery(id+"F0.imprint","IMPRINT",EDGE,{"disambiguationData":[TD([[makeQuery(id+"F0.imprint","INTERSECT",VERTEX,{"derivedFrom":[sQuery(id+"F0.wireOp",EDGE,"E5"),subQ1]}),1.0]])],"derivedFrom":subQ1})])]}),makeQuery(id+"F3.opExtrude","SWEPT_FACE",FACE,{"disambiguationData":[OSD([subQ0])]})]})])]}),makeQuery(id+"F8.opExtrude","SWEPT_FACE",FACE,{"disambiguationData":[OSD([sQuery(id+"F7.wireOp",EDGE,"E23")])]})]});}
            fillet(context, id + "F9", {"entities" : qUnion([Q0, Q1, Q2, Q3, Q4, Q5, Q6, Q7, Q8, Q9, Q10, Q11, Q12, Q13, Q14, Q15, Q16, Q17, Q18, Q19]), "tangentPropagation" : true, "radius" : 50 * mm, "defaultsChanged" : false, "vertexSettings" : [], "allowEdgeOverflow" : false});
        }
    });
